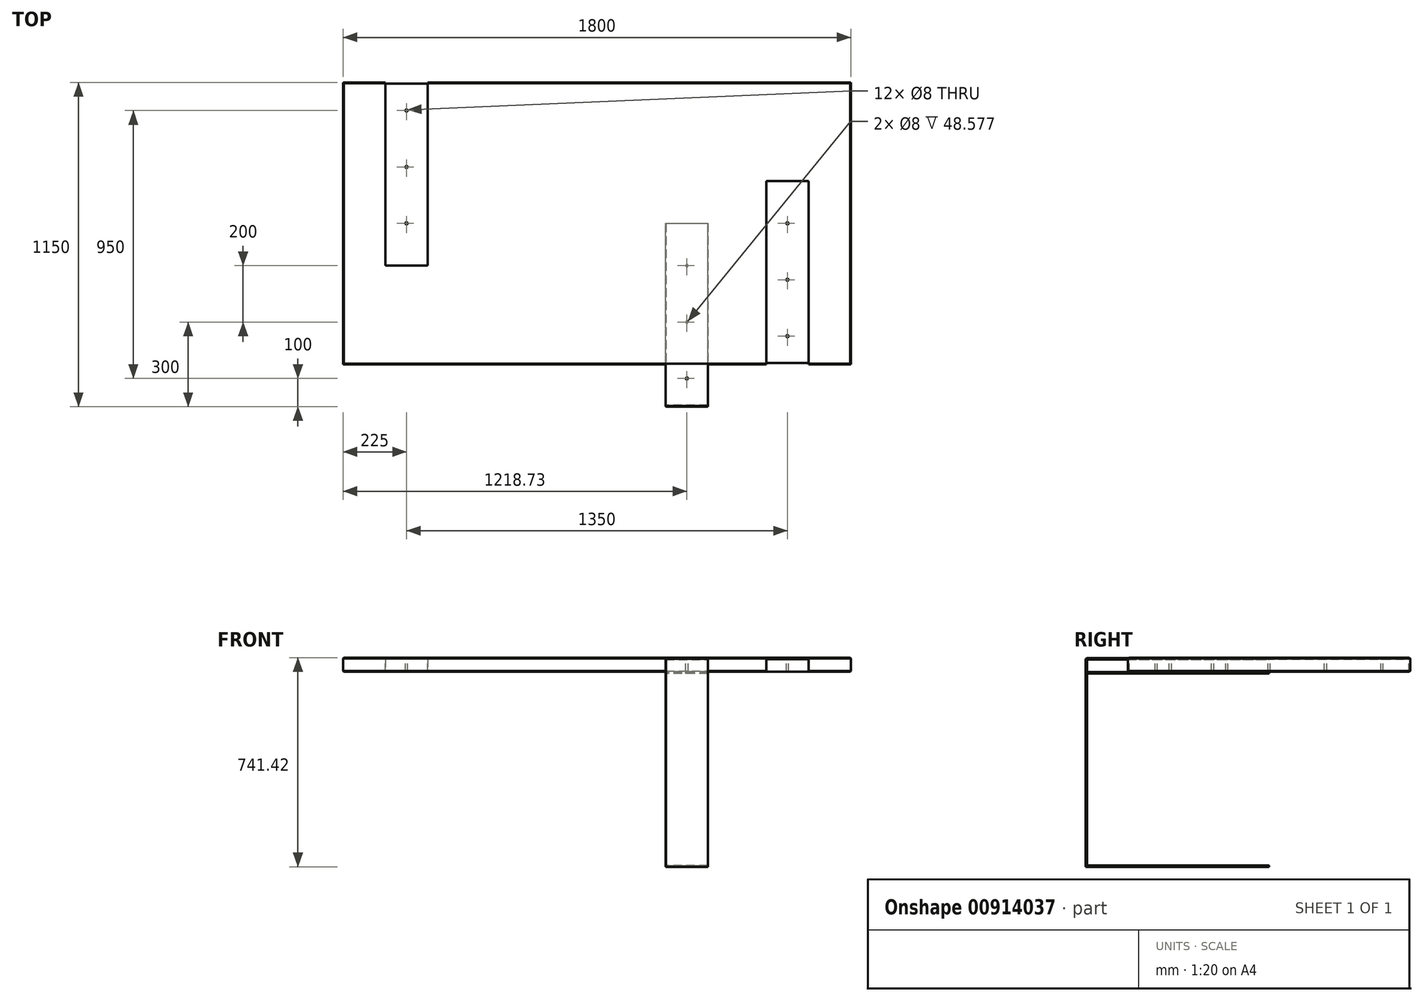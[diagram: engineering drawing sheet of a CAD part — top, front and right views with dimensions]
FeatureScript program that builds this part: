
annotation { "Feature Type Name" : "Feature", "Feature Type Description" : "" }
export const myFeature = defineFeature(function(context is Context, id is Id, definition is map)
    precondition{}
    {
        {
            var Q0;
            Q0=qCreatedBy(makeId("Top.planeOp"),FACE);
            var sketch = newSketch(context, id + "F0", { "sketchPlane" : qUnion([Q0])});
            skLineSegment(sketch, "E0.bottom", {"start": v(-900, 500) * mm, "end": v(900, 500) * mm});
            skLineSegment(sketch, "E0.top", {"start": v(-900, -500) * mm, "end": v(900, -500) * mm});
            skLineSegment(sketch, "E0.left", {"start": v(-900, 500) * mm, "end": v(-900, -500) * mm});
            skLineSegment(sketch, "E0.right", {"start": v(900, 500) * mm, "end": v(900, -500) * mm});
            skPoint(sketch, "E0.middle", {"position": v(0, 0) * mm});
            skSolve(sketch);
        }
        {
            var Q0;
            Q0 = qSketchRegion(id + "F0", true);
            extrude(context, id + "F1", {"entities" : qUnion([Q0]), "depth" : 50 * mm, "offsetDistance" : 25 * mm});
        }
        {
            var Q0;
            Q0=makeQuery(id+"F1.opExtrude","SWEPT_FACE",FACE,{"disambiguationData":[OSD([sQuery(id+"F0.wireOp",EDGE,"E0.top")])]});
            var sketch = newSketch(context, id + "F2", { "sketchPlane" : qUnion([Q0])});
            skLineSegment(sketch, "E1.bottom", {"start": v(600, 45) * mm, "end": v(750, 45) * mm});
            skLineSegment(sketch, "E1.top", {"start": v(600, 55) * mm, "end": v(750, 55) * mm});
            skLineSegment(sketch, "E1.left", {"start": v(600, 45) * mm, "end": v(600, 55) * mm});
            skLineSegment(sketch, "E1.right", {"start": v(750, 45) * mm, "end": v(750, 55) * mm});
            skPoint(sketch, "E1.middle", {"position": v(675, 50) * mm});
            skSolve(sketch);
        }
        {
            var Q0;
            Q0 = qSketchRegion(id + "F2", true);
            extrude(context, id + "F3", {"entities" : qUnion([Q0]), "operationType" : NewBodyOperationType.REMOVE, "oppositeDirection" : true, "depth" : 650 * mm, "offsetDistance" : 25 * mm});
        }
        {
            var Q0;
            Q0=makeQuery(id+"F1.opExtrude","SWEPT_FACE",FACE,{"disambiguationData":[OSD([sQuery(id+"F0.wireOp",EDGE,"E0.bottom")])]});
            var sketch = newSketch(context, id + "F4", { "sketchPlane" : qUnion([Q0])});
            skLineSegment(sketch, "E2.bottom", {"start": v(750, 50) * mm, "end": v(600, 50) * mm});
            skLineSegment(sketch, "E2.top", {"start": v(750, 45) * mm, "end": v(600, 45) * mm});
            skLineSegment(sketch, "E2.left", {"start": v(750, 50) * mm, "end": v(750, 45) * mm});
            skLineSegment(sketch, "E2.right", {"start": v(600, 50) * mm, "end": v(600, 45) * mm});
            skSolve(sketch);
        }
        {
            var Q0;
            Q0 = qSketchRegion(id + "F4", true);
            extrude(context, id + "F5", {"entities" : qUnion([Q0]), "operationType" : NewBodyOperationType.REMOVE, "oppositeDirection" : true, "depth" : 650 * mm, "offsetDistance" : 25 * mm});
        }
        {
            var Q0;
            Q0=makeQuery(id+"F3.boolean.opBoolean","COPY",FACE,{"derivedFrom":makeQuery(id+"F3.opExtrude","SWEPT_FACE",FACE,{"disambiguationData":[OSD([sQuery(id+"F2.wireOp",EDGE,"E1.bottom")])]})});
            var sketch = newSketch(context, id + "F6", { "sketchPlane" : qUnion([Q0])});
            skCircle(sketch, "E3", {"center": v(675, 0) * mm, "radius": 4 * mm});
            skCircle(sketch, "E4", {"center": v(675, -200) * mm, "radius": 4 * mm});
            skCircle(sketch, "E5", {"center": v(675, -400) * mm, "radius": 4 * mm});
            skCircle(sketch, "E6", {"center": v(-675, 400) * mm, "radius": 4 * mm});
            skCircle(sketch, "E7", {"center": v(-675, 200) * mm, "radius": 4 * mm});
            skCircle(sketch, "E8", {"center": v(-675, 0) * mm, "radius": 4 * mm});
            skSolve(sketch);
        }
        {
            var Q0;
            Q0 = qSketchRegion(id + "F6", true);
            extrude(context, id + "F7", {"entities" : qUnion([Q0]), "operationType" : NewBodyOperationType.REMOVE, "oppositeDirection" : true, "depth" : 50 * mm, "offsetDistance" : 25 * mm});
        }
        {
            var Q0;
            Q0=qCreatedBy(makeId("Front.planeOp"),FACE);
            var sketch = newSketch(context, id + "F8", { "sketchPlane" : qUnion([Q0])});
            skLineSegment(sketch, "E9.bottom", {"start": v(243.74, 48.58) * mm, "end": v(393.74, 48.58) * mm});
            skLineSegment(sketch, "E9.top", {"start": v(243.74, 43.58) * mm, "end": v(393.74, 43.58) * mm});
            skLineSegment(sketch, "E9.left", {"start": v(243.74, 48.58) * mm, "end": v(243.74, 43.58) * mm});
            skLineSegment(sketch, "E9.right", {"start": v(393.74, 48.58) * mm, "end": v(393.74, 43.58) * mm});
            skSolve(sketch);
        }
        {
            var Q0;
            Q0 = qSketchRegion(id + "F8", true);
            extrude(context, id + "F9", {"entities" : qUnion([Q0]), "depth" : 650 * mm, "offsetDistance" : 25 * mm});
        }
        {
            var Q0;
            Q0=makeQuery(id+"F9.opExtrude","SWEPT_FACE",FACE,{"disambiguationData":[OSD([sQuery(id+"F8.wireOp",EDGE,"E9.top")])]});
            var sketch = newSketch(context, id + "F10", { "sketchPlane" : qUnion([Q0])});
            skLineSegment(sketch, "E10.bottom", {"start": v(243.74, 650) * mm, "end": v(393.74, 650) * mm});
            skLineSegment(sketch, "E10.top", {"start": v(243.74, 645) * mm, "end": v(393.74, 645) * mm});
            skLineSegment(sketch, "E10.left", {"start": v(243.74, 650) * mm, "end": v(243.74, 645) * mm});
            skLineSegment(sketch, "E10.right", {"start": v(393.74, 650) * mm, "end": v(393.74, 645) * mm});
            skSolve(sketch);
        }
        {
            var Q0;
            Q0 = qSketchRegion(id + "F10", true);
            extrude(context, id + "F11", {"entities" : qUnion([Q0]), "operationType" : NewBodyOperationType.ADD, "depth" : 735 * mm, "offsetDistance" : 25 * mm});
        }
        {
            var Q0;
            Q0=makeQuery(id+"F11.opExtrude","SWEPT_FACE",FACE,{"disambiguationData":[OSD([sQuery(id+"F10.wireOp",EDGE,"E10.top")])]});
            var sketch = newSketch(context, id + "F12", { "sketchPlane" : qUnion([Q0])});
            skLineSegment(sketch, "E11.bottom", {"start": v(-393.74, -691.42) * mm, "end": v(-243.74, -691.42) * mm});
            skLineSegment(sketch, "E11.top", {"start": v(-393.74, -686.42) * mm, "end": v(-243.74, -686.42) * mm});
            skLineSegment(sketch, "E11.left", {"start": v(-393.74, -691.42) * mm, "end": v(-393.74, -686.42) * mm});
            skLineSegment(sketch, "E11.right", {"start": v(-243.74, -691.42) * mm, "end": v(-243.74, -686.42) * mm});
            skSolve(sketch);
        }
        {
            var Q0;
            Q0 = qSketchRegion(id + "F12", true);
            extrude(context, id + "F13", {"entities" : qUnion([Q0]), "operationType" : NewBodyOperationType.ADD, "depth" : 645 * mm, "offsetDistance" : 25 * mm});
        }
        {
            var Q0;
            Q0=makeQuery(id+"F11.opExtrude","SWEPT_FACE",FACE,{"disambiguationData":[OSD([sQuery(id+"F10.wireOp",EDGE,"E10.top")])]});
            var sketch = newSketch(context, id + "F14", { "sketchPlane" : qUnion([Q0])});
            skLineSegment(sketch, "E12.bottom", {"start": v(-393.74, -1.42) * mm, "end": v(-243.74, -1.42) * mm});
            skLineSegment(sketch, "E12.top", {"start": v(-393.74, -6.42) * mm, "end": v(-243.74, -6.42) * mm});
            skLineSegment(sketch, "E12.left", {"start": v(-393.74, -1.42) * mm, "end": v(-393.74, -6.42) * mm});
            skLineSegment(sketch, "E12.right", {"start": v(-243.74, -1.42) * mm, "end": v(-243.74, -6.42) * mm});
            skSolve(sketch);
        }
        {
            var Q0;
            Q0 = qSketchRegion(id + "F14", true);
            extrude(context, id + "F15", {"entities" : qUnion([Q0]), "operationType" : NewBodyOperationType.ADD, "depth" : 645 * mm, "offsetDistance" : 25 * mm});
        }
        {
            var Q0;
            Q0=makeQuery(id+"F9.opExtrude","SWEPT_FACE",FACE,{"disambiguationData":[OSD([sQuery(id+"F8.wireOp",EDGE,"E9.bottom")])]});
            var sketch = newSketch(context, id + "F16", { "sketchPlane" : qUnion([Q0])});
            skCircle(sketch, "E13", {"center": v(318.74, -150) * mm, "radius": 4 * mm});
            skPoint(sketch, "E13.centerSnap0", {"position": v(318.74, 0) * mm});
            skCircle(sketch, "E14", {"center": v(318.74, -350) * mm, "radius": 4 * mm});
            skCircle(sketch, "E15", {"center": v(318.74, -550) * mm, "radius": 4 * mm});
            skSolve(sketch);
        }
        {
            var Q0;
            Q0 = qSketchRegion(id + "F16", true);
            extrude(context, id + "F17", {"entities" : qUnion([Q0]), "operationType" : NewBodyOperationType.REMOVE, "oppositeDirection" : true, "depth" : 80 * mm, "offsetDistance" : 25 * mm});
        }
        {
            var Q0;
            Q0=makeQuery(id+"F3.boolean.opBoolean","COPY",FACE,{"derivedFrom":makeQuery(id+"F3.opExtrude","SWEPT_FACE",FACE,{"disambiguationData":[OSD([sQuery(id+"F2.wireOp",EDGE,"E1.bottom")])]})});
            var sketch = newSketch(context, id + "F18", { "sketchPlane" : qUnion([Q0])});
            skLineSegment(sketch, "E16.bottom", {"start": v(600, -500) * mm, "end": v(750, -500) * mm});
            skLineSegment(sketch, "E16.top", {"start": v(600, -495) * mm, "end": v(750, -495) * mm});
            skLineSegment(sketch, "E16.left", {"start": v(600, -500) * mm, "end": v(600, -495) * mm});
            skLineSegment(sketch, "E16.right", {"start": v(750, -500) * mm, "end": v(750, -495) * mm});
            skSolve(sketch);
        }
        {
            var Q0;
            Q0 = qSketchRegion(id + "F18", true);
            extrude(context, id + "F19", {"entities" : qUnion([Q0]), "operationType" : NewBodyOperationType.REMOVE, "oppositeDirection" : true, "depth" : 100 * mm, "offsetDistance" : 25 * mm});
        }
        {
            var Q0;
            Q0=makeQuery(id+"F5.boolean.opBoolean","COPY",FACE,{"derivedFrom":makeQuery(id+"F5.opExtrude","SWEPT_FACE",FACE,{"disambiguationData":[OSD([sQuery(id+"F4.wireOp",EDGE,"E2.top")])]})});
            var sketch = newSketch(context, id + "F20", { "sketchPlane" : qUnion([Q0])});
            skLineSegment(sketch, "E17.bottom", {"start": v(-600, 500) * mm, "end": v(-750, 500) * mm});
            skLineSegment(sketch, "E17.top", {"start": v(-600, 495) * mm, "end": v(-750, 495) * mm});
            skLineSegment(sketch, "E17.left", {"start": v(-600, 500) * mm, "end": v(-600, 495) * mm});
            skLineSegment(sketch, "E17.right", {"start": v(-750, 500) * mm, "end": v(-750, 495) * mm});
            skSolve(sketch);
        }
        {
            var Q0;
            Q0 = qSketchRegion(id + "F20", true);
            extrude(context, id + "F21", {"entities" : qUnion([Q0]), "operationType" : NewBodyOperationType.REMOVE, "oppositeDirection" : true, "depth" : 100 * mm, "offsetDistance" : 25 * mm});
        }
        {
            var Q0;
            {var subQ0=sQuery(id+"F0.wireOp",EDGE,"E0.bottom");var subQ1=sQuery(id+"F0.wireOp",EDGE,"E0.right");Q0=makeQuery(id+"F5.boolean.opBoolean","SPLIT",EDGE,{"disambiguationData":[TD([makeQuery(id+"F1.opExtrude","SWEPT_FACE",FACE,{"disambiguationData":[OSD([subQ1])]})])],"derivedFrom":makeQuery(id+"F1.opExtrude","CAP_EDGE",EDGE,{"disambiguationData":[OSD([subQ0])],"isStart":false})});}
            var Q1;
            {var subQ0=sQuery(id+"F0.wireOp",EDGE,"E0.bottom");var subQ1=sQuery(id+"F0.wireOp",EDGE,"E0.left");Q1=makeQuery(id+"F5.boolean.opBoolean","SPLIT",EDGE,{"disambiguationData":[TD([makeQuery(id+"F1.opExtrude","SWEPT_FACE",FACE,{"disambiguationData":[OSD([subQ1])]})])],"derivedFrom":makeQuery(id+"F1.opExtrude","CAP_EDGE",EDGE,{"disambiguationData":[OSD([subQ0])],"isStart":false})});}
            var Q2;
            Q2=makeQuery(id+"F1.opExtrude","CAP_EDGE",EDGE,{"disambiguationData":[OSD([sQuery(id+"F0.wireOp",EDGE,"E0.left")])],"isStart":false});
            var Q3;
            {var subQ0=sQuery(id+"F0.wireOp",EDGE,"E0.left");var subQ1=sQuery(id+"F0.wireOp",EDGE,"E0.top");Q3=makeQuery(id+"F3.boolean.opBoolean","SPLIT",EDGE,{"disambiguationData":[TD([makeQuery(id+"F1.opExtrude","SWEPT_FACE",FACE,{"disambiguationData":[OSD([subQ0])]})])],"derivedFrom":makeQuery(id+"F1.opExtrude","CAP_EDGE",EDGE,{"disambiguationData":[OSD([subQ1])],"isStart":false})});}
            var Q4;
            {var subQ0=sQuery(id+"F0.wireOp",EDGE,"E0.right");var subQ1=sQuery(id+"F0.wireOp",EDGE,"E0.top");Q4=makeQuery(id+"F3.boolean.opBoolean","SPLIT",EDGE,{"disambiguationData":[TD([makeQuery(id+"F1.opExtrude","SWEPT_FACE",FACE,{"disambiguationData":[OSD([subQ0])]})])],"derivedFrom":makeQuery(id+"F1.opExtrude","CAP_EDGE",EDGE,{"disambiguationData":[OSD([subQ1])],"isStart":false})});}
            var Q5;
            {var subQ0=sQuery(id+"F0.wireOp",EDGE,"E0.right");var subQ1=sQuery(id+"F0.wireOp",EDGE,"E0.top");Q5=makeQuery(id+"F19.boolean.opBoolean","SPLIT",EDGE,{"disambiguationData":[TD([makeQuery(id+"F1.opExtrude","SWEPT_FACE",FACE,{"disambiguationData":[OSD([subQ0])]})])],"derivedFrom":makeQuery(id+"F1.opExtrude","CAP_EDGE",EDGE,{"disambiguationData":[OSD([subQ1])],"isStart":true})});}
            var Q6;
            {var subQ0=sQuery(id+"F0.wireOp",EDGE,"E0.left");var subQ1=sQuery(id+"F0.wireOp",EDGE,"E0.top");Q6=makeQuery(id+"F19.boolean.opBoolean","SPLIT",EDGE,{"disambiguationData":[TD([makeQuery(id+"F1.opExtrude","SWEPT_FACE",FACE,{"disambiguationData":[OSD([subQ0])]})])],"derivedFrom":makeQuery(id+"F1.opExtrude","CAP_EDGE",EDGE,{"disambiguationData":[OSD([subQ1])],"isStart":true})});}
            var Q7;
            Q7=makeQuery(id+"F1.opExtrude","CAP_EDGE",EDGE,{"disambiguationData":[OSD([sQuery(id+"F0.wireOp",EDGE,"E0.left")])],"isStart":true});
            var Q8;
            {var subQ0=sQuery(id+"F0.wireOp",EDGE,"E0.left");var subQ1=sQuery(id+"F0.wireOp",EDGE,"E0.bottom");Q8=makeQuery(id+"F21.boolean.opBoolean","SPLIT",EDGE,{"disambiguationData":[TD([makeQuery(id+"F1.opExtrude","SWEPT_FACE",FACE,{"disambiguationData":[OSD([subQ0])]})])],"derivedFrom":makeQuery(id+"F1.opExtrude","CAP_EDGE",EDGE,{"disambiguationData":[OSD([subQ1])],"isStart":true})});}
            var Q9;
            {var subQ0=sQuery(id+"F0.wireOp",EDGE,"E0.right");var subQ1=sQuery(id+"F0.wireOp",EDGE,"E0.bottom");Q9=makeQuery(id+"F21.boolean.opBoolean","SPLIT",EDGE,{"disambiguationData":[TD([makeQuery(id+"F1.opExtrude","SWEPT_FACE",FACE,{"disambiguationData":[OSD([subQ0])]})])],"derivedFrom":makeQuery(id+"F1.opExtrude","CAP_EDGE",EDGE,{"disambiguationData":[OSD([subQ1])],"isStart":true})});}
            var Q10;
            Q10=makeQuery(id+"F1.opExtrude","CAP_EDGE",EDGE,{"disambiguationData":[OSD([sQuery(id+"F0.wireOp",EDGE,"E0.right")])],"isStart":false});
            var Q11;
            Q11=makeQuery(id+"F1.opExtrude","CAP_EDGE",EDGE,{"disambiguationData":[OSD([sQuery(id+"F0.wireOp",EDGE,"E0.right")])],"isStart":true});
            chamfer(context, id + "F22", {"entities" : qUnion([Q0, Q1, Q2, Q3, Q4, Q5, Q6, Q7, Q8, Q9, Q10, Q11]), "width" : 3 * mm, "tangentPropagation" : true});
        }
        {
            var Q0;
            Q0=makeQuery(id+"F9.opExtrude","CAP_EDGE",EDGE,{"disambiguationData":[OSD([sQuery(id+"F8.wireOp",EDGE,"E9.bottom")])],"isStart":false});
            chamfer(context, id + "F23", {"entities" : qUnion([Q0]), "width" : 3 * mm, "tangentPropagation" : true});
        }
        {
            var Q0;
            Q0=makeQuery(id+"F11.boolean.opBoolean","MERGE",EDGE,{"derivedFrom":[makeQuery(id+"F9.opExtrude","CAP_EDGE",EDGE,{"disambiguationData":[OSD([sQuery(id+"F8.wireOp",EDGE,"E9.right")])],"isStart":false}),makeQuery(id+"F11.opExtrude","SWEPT_EDGE",EDGE,{"disambiguationData":[OSD([sQuery(id+"F10.wireOp",EDGE,"E10.bottom"),sQuery(id+"F10.wireOp",EDGE,"E10.right")])]})]});
            var Q1;
            Q1=makeQuery(id+"F11.boolean.opBoolean","MERGE",EDGE,{"derivedFrom":[makeQuery(id+"F9.opExtrude","CAP_EDGE",EDGE,{"disambiguationData":[OSD([sQuery(id+"F8.wireOp",EDGE,"E9.left")])],"isStart":false}),makeQuery(id+"F11.opExtrude","SWEPT_EDGE",EDGE,{"disambiguationData":[OSD([sQuery(id+"F10.wireOp",EDGE,"E10.bottom"),sQuery(id+"F10.wireOp",EDGE,"E10.left")])]})]});
            var Q2;
            {var subQ0=sQuery(id+"F10.wireOp",EDGE,"E10.left");var subQ1=sQuery(id+"F10.wireOp",EDGE,"E10.top");var subQ2=sQuery(id+"F8.wireOp",EDGE,"E9.left");Q2=makeQuery(id+"F15.boolean.opBoolean","SPLIT",EDGE,{"disambiguationData":[TD([makeQuery(id+"F13.opExtrude","SWEPT_FACE",FACE,{"disambiguationData":[OSD([sQuery(id+"F12.wireOp",EDGE,"E11.top")])]})])],"derivedFrom":makeQuery(id+"F11.opExtrude","SWEPT_EDGE",EDGE,{"disambiguationData":[OSD([sQuery(id+"F8.wireOp",EDGE,"E9.top"),subQ2,subQ1,subQ0])]})});}
            var Q3;
            {var subQ0=sQuery(id+"F10.wireOp",EDGE,"E10.right");var subQ1=sQuery(id+"F10.wireOp",EDGE,"E10.top");var subQ2=sQuery(id+"F8.wireOp",EDGE,"E9.right");Q3=makeQuery(id+"F15.boolean.opBoolean","SPLIT",EDGE,{"disambiguationData":[TD([makeQuery(id+"F13.opExtrude","SWEPT_FACE",FACE,{"disambiguationData":[OSD([sQuery(id+"F12.wireOp",EDGE,"E11.top")])]})])],"derivedFrom":makeQuery(id+"F11.opExtrude","SWEPT_EDGE",EDGE,{"disambiguationData":[OSD([sQuery(id+"F8.wireOp",EDGE,"E9.top"),subQ2,subQ1,subQ0])]})});}
            var Q4;
            Q4=makeQuery(id+"F13.opExtrude","SWEPT_EDGE",EDGE,{"disambiguationData":[OSD([sQuery(id+"F8.wireOp",EDGE,"E9.top"),sQuery(id+"F8.wireOp",EDGE,"E9.right"),sQuery(id+"F10.wireOp",EDGE,"E10.top"),sQuery(id+"F10.wireOp",EDGE,"E10.right"),sQuery(id+"F12.wireOp",EDGE,"E11.top"),sQuery(id+"F12.wireOp",EDGE,"E11.left")])]});
            var Q5;
            Q5=makeQuery(id+"F13.opExtrude","CAP_EDGE",EDGE,{"disambiguationData":[OSD([sQuery(id+"F12.wireOp",EDGE,"E11.top")])],"isStart":false});
            var Q6;
            Q6=makeQuery(id+"F13.opExtrude","SWEPT_EDGE",EDGE,{"disambiguationData":[OSD([sQuery(id+"F8.wireOp",EDGE,"E9.top"),sQuery(id+"F8.wireOp",EDGE,"E9.left"),sQuery(id+"F10.wireOp",EDGE,"E10.top"),sQuery(id+"F10.wireOp",EDGE,"E10.left"),sQuery(id+"F12.wireOp",EDGE,"E11.top"),sQuery(id+"F12.wireOp",EDGE,"E11.right")])]});
            chamfer(context, id + "F24", {"entities" : qUnion([Q0, Q1, Q2, Q3, Q4, Q5, Q6]), "width" : 1 * mm, "tangentPropagation" : true});
        }
    });
